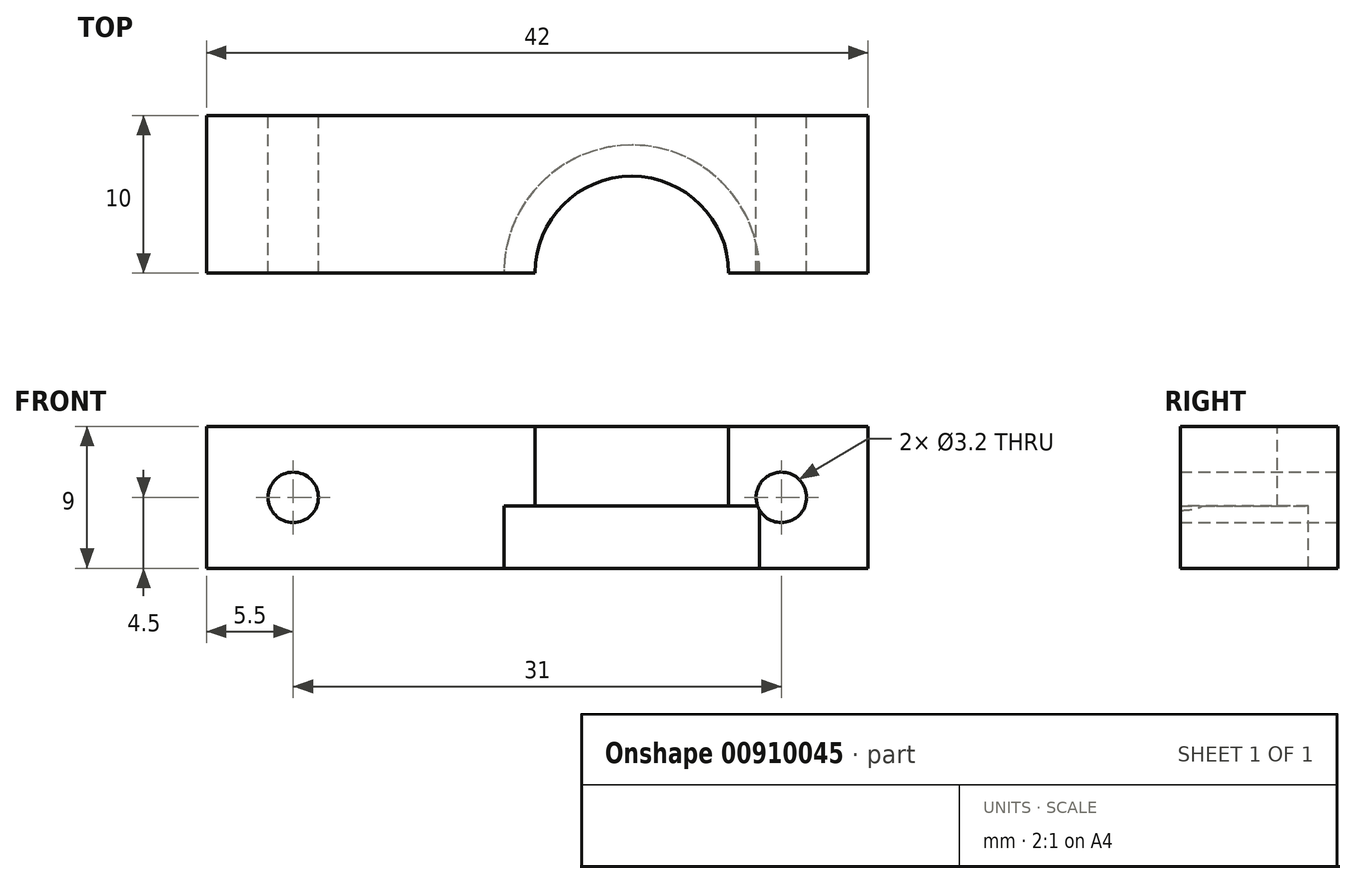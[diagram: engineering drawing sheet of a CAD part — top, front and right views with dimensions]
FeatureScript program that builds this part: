
annotation { "Feature Type Name" : "Feature", "Feature Type Description" : "" }
export const myFeature = defineFeature(function(context is Context, id is Id, definition is map)
    precondition{}
    {
        {
            var Q0;
            Q0=qCreatedBy(makeId("Top.planeOp"),FACE);
            var sketch = newSketch(context, id + "F0", { "sketchPlane" : qUnion([Q0])});
            skCircle(sketch, "E0", {"center": v(0, 0) * mm, "radius": 6.15 * mm});
            skCircle(sketch, "E1", {"center": v(0, 0) * mm, "radius": 8.12 * mm});
            skLineSegment(sketch, "E2", {"start": v(0, 0) * mm, "end": v(-6, 0) * mm});
            skLineSegment(sketch, "E3", {"start": v(-6, 0) * mm, "end": v(-6, -10) * mm});
            skLineSegment(sketch, "E4", {"start": v(-6, -10) * mm, "end": v(15, -10) * mm});
            skLineSegment(sketch, "E5", {"start": v(-6, -10) * mm, "end": v(-27, -10) * mm});
            skLineSegment(sketch, "E6", {"start": v(-27, -10) * mm, "end": v(-27, 0) * mm});
            skLineSegment(sketch, "E7", {"start": v(-27, 0) * mm, "end": v(-6, 0) * mm});
            skLineSegment(sketch, "E8", {"start": v(6.15, 0) * mm, "end": v(15, 0) * mm});
            skLineSegment(sketch, "E9", {"start": v(15, 0) * mm, "end": v(15, -10) * mm});
            skLineSegment(sketch, "E10", {"start": v(-27, 0) * mm, "end": v(-27, 10) * mm});
            skLineSegment(sketch, "E11", {"start": v(-27, 10) * mm, "end": v(15, 10) * mm});
            skLineSegment(sketch, "E12", {"start": v(15, 10) * mm, "end": v(15, 0) * mm});
            skSolve(sketch);
        }
        {
            var Q0;
            {var subQ6=sQuery(id+"F0.wireOp",EDGE,"E10");Q0=makeQuery(id+"F0.imprint","IMPRINT",FACE,{"disambiguationData":[TD([[makeQuery(id+"F0.imprint","IMPRINT",EDGE,{"derivedFrom":subQ6}),-1.0]])]});}
            extrude(context, id + "F1", {"entities" : qUnion([Q0]), "oppositeDirection" : true, "depth" : 10 * mm, "offsetDistance" : 25 * mm});
        }
        {
            var Q0;
            {var subQ0=sQuery(id+"F0.wireOp",EDGE,"E7");var subQ5=sQuery(id+"F0.wireOp",EDGE,"E1");var subQ6=makeQuery(id+"F0.imprint","INTERSECT",VERTEX,{"derivedFrom":[subQ5,subQ0]});Q0=makeQuery(id+"F0.imprint","IMPRINT",FACE,{"disambiguationData":[TD([[makeQuery(id+"F0.imprint","IMPRINT",EDGE,{"disambiguationData":[TD([[subQ6,1.0]])],"derivedFrom":subQ5}),1.0]])]});}
            extrude(context, id + "F2", {"entities" : qUnion([Q0]), "operationType" : NewBodyOperationType.ADD, "oppositeDirection" : true, "depth" : (10 - 3.7) * mm, "offsetDistance" : 25 * mm});
        }
        {
            var Q0;
            Q0=makeQuery(id+"F1.opExtrude","SWEPT_FACE",FACE,{"disambiguationData":[OSD([sQuery(id+"F0.wireOp",EDGE,"E11")])]});
            var sketch = newSketch(context, id + "F3", { "sketchPlane" : qUnion([Q0])});
            skLineSegment(sketch, "E13", {"start": v(6, 0) * mm, "end": v(6, -5.5) * mm});
            skLineSegment(sketch, "E14", {"start": v(6, -5.5) * mm, "end": v(-9.5, -5.5) * mm});
            skLineSegment(sketch, "E15", {"start": v(6, -5.5) * mm, "end": v(21.5, -5.5) * mm});
            skLineSegment(sketch, "E16", {"start": v(6, 0) * mm, "end": v(6, -42) * mm});
            skLineSegment(sketch, "E17", {"start": v(6, -21) * mm, "end": v(6, -5.5) * mm});
            skCircle(sketch, "E18", {"center": v(-9.5, -5.5) * mm, "radius": 1.6 * mm});
            skCircle(sketch, "E19", {"center": v(21.5, -5.5) * mm, "radius": 1.6 * mm});
            skSolve(sketch);
        }
        {
            var Q0;
            Q0=makeQuery(id+"F3.imprint","IMPRINT",FACE,{"disambiguationData":[TD([[makeQuery(id+"F3.imprint","IMPRINT",EDGE,{"derivedFrom":sQuery(id+"F3.wireOp",EDGE,"E18")}),1.0]])]});
            var Q1;
            Q1=makeQuery(id+"F3.imprint","IMPRINT",FACE,{"disambiguationData":[TD([[makeQuery(id+"F3.imprint","IMPRINT",EDGE,{"derivedFrom":sQuery(id+"F3.wireOp",EDGE,"E19")}),1.0]])]});
            extrude(context, id + "F4", {"entities" : qUnion([Q0, Q1]), "operationType" : NewBodyOperationType.REMOVE, "oppositeDirection" : true, "depth" : 25 * mm, "offsetDistance" : 25 * mm});
        }
        {
            var Q0;
            {var subQ4=sQuery(id+"F0.wireOp",EDGE,"E10");Q0=makeQuery(id+"F0.imprint","IMPRINT",FACE,{"disambiguationData":[TD([[makeQuery(id+"F0.imprint","IMPRINT",EDGE,{"derivedFrom":subQ4}),-1.0]])]});}
            var Q1;
            {var subQ0=sQuery(id+"F0.wireOp",EDGE,"E8");var subQ1=sQuery(id+"F0.wireOp",EDGE,"E0");var subQ2=makeQuery(id+"F0.imprint","INTERSECT",VERTEX,{"derivedFrom":[subQ1,subQ0]});Q1=makeQuery(id+"F0.imprint","IMPRINT",FACE,{"disambiguationData":[TD([[makeQuery(id+"F0.imprint","IMPRINT",EDGE,{"disambiguationData":[TD([[subQ2,-1.0]])],"derivedFrom":subQ1}),-1.0]])]});}
            extrude(context, id + "F5", {"entities" : qUnion([Q0, Q1]), "operationType" : NewBodyOperationType.REMOVE, "oppositeDirection" : true, "depth" : 1 * mm, "offsetDistance" : 25 * mm});
        }
        {
            var Q0;
            Q0=makeQuery(id+"F2.opExtrude","CAP_FACE",FACE,{"disambiguationData":[OSD([sQuery(id+"F0.wireOp",EDGE,"E0"),sQuery(id+"F0.wireOp",EDGE,"E1"),sQuery(id+"F0.wireOp",EDGE,"E7"),sQuery(id+"F0.wireOp",EDGE,"E8")])],"isStart":false});
            extrude(context, id + "F6", {"entities" : qUnion([Q0]), "operationType" : NewBodyOperationType.REMOVE, "oppositeDirection" : true, "depth" : .25 * mm, "offsetDistance" : 25 * mm});
        }
    });
